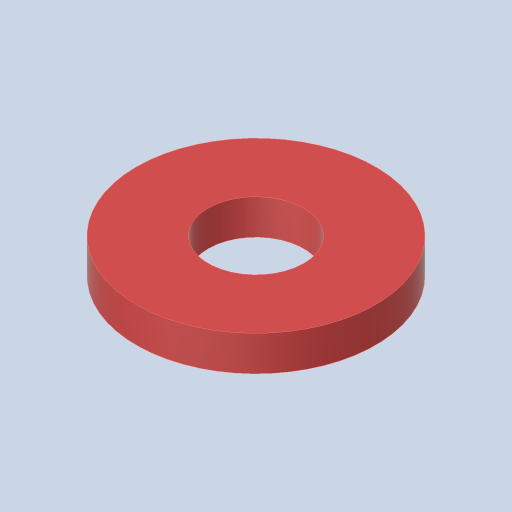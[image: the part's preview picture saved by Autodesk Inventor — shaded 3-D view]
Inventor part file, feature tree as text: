
AUTODESK INVENTOR PART (.ipt)
format: ipt  version: 2023.4 (Build 274418000, 418)  size: 92,672 bytes
history: native  units: in
note: dims shown in document units (in); Inventor stores cm internally (conversion verified against a paired STEP export)
features: extrude x1, sketch x1
ambient origin geometry x8: Origin, YZ Plane, XZ Plane, XY Plane, X Axis, Y Axis, Z Axis, Center Point
bodies: Solid1 (feature_tree)
feature tree (2):
  extrude  "Extrusion1"  Depth=0.11in
  sketch  "Sketch1"  dims[d0=0.3in d1=0.75in d2=0.11in d3=0.0in]
